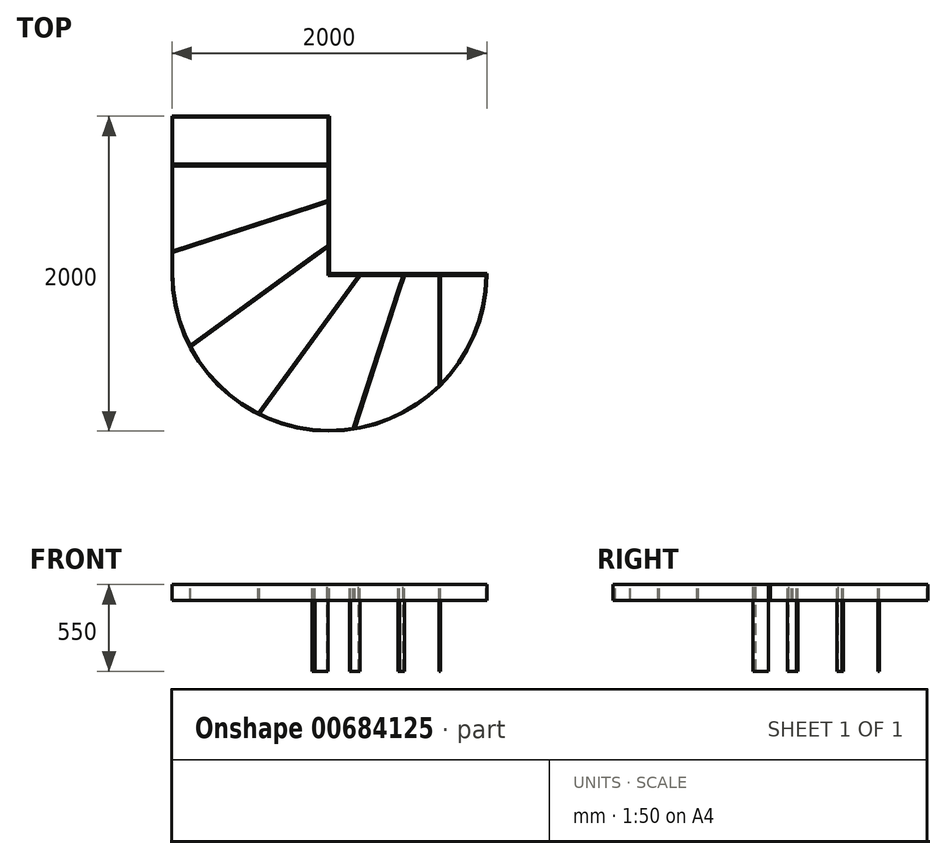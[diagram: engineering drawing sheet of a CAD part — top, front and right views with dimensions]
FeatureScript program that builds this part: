
annotation { "Feature Type Name" : "Feature", "Feature Type Description" : "" }
export const myFeature = defineFeature(function(context is Context, id is Id, definition is map)
    precondition{}
    {
        {
            var Q0;
            Q0=qCreatedBy(makeId("Top.planeOp"),FACE);
            var sketch = newSketch(context, id + "F0", { "sketchPlane" : qUnion([Q0])});
            skLineSegment(sketch, "E0", {"start": v(0, 0) * mm, "end": v(-1000, 0) * mm});
            skLineSegment(sketch, "E1", {"start": v(-1000, 0) * mm, "end": v(-1000, -1000) * mm});
            skLineSegment(sketch, "E2", {"start": v(0, 0) * mm, "end": v(0, -1000) * mm});
            skLineSegment(sketch, "E3", {"start": v(0, -1000) * mm, "end": v(1000, -1000) * mm});
            skArc(sketch, "E4", {"start": v(-1000, -1000) * mm, "mid": v(0, -2000) * mm, "end": v(1000, -1000) * mm});
            skLineSegment(sketch, "E5", {"start": v(-1000, -1000) * mm, "end": v(0, -1000) * mm, "construction": true});
            skLineSegment(sketch, "E6.0", {"start": v(-10, -1010) * mm, "end": v(1000, -1010) * mm});
            skLineSegment(sketch, "E6.1", {"start": v(-10, 0) * mm, "end": v(-10, -1010) * mm});
            skArc(sketch, "E7.0", {"start": v(-995, -1000) * mm, "mid": v(-5, -1994.99) * mm, "end": v(994.95, -1010) * mm});
            skLineSegment(sketch, "E7.1", {"start": v(-995, -5) * mm, "end": v(-995, -1000) * mm});
            skLineSegment(sketch, "E7.2", {"start": v(-10, -5) * mm, "end": v(-995, -5) * mm});
            skLineSegment(sketch, "E8", {"start": v(700, -310) * mm, "end": v(0, -310) * mm, "construction": true});
            skLineSegment(sketch, "E9", {"start": v(700, -310) * mm, "end": v(700, -1010) * mm, "construction": true});
            skLineSegment(sketch, "E10", {"start": v(-10, -310) * mm, "end": v(-995, -310) * mm, "construction": true});
            skLineSegment(sketch, "E11", {"start": v(700, -1010) * mm, "end": v(700, -1707.12) * mm, "construction": true});
            skLineSegment(sketch, "E12", {"start": v(700, -310) * mm, "end": v(0, -537.44) * mm, "construction": true});
            skLineSegment(sketch, "E13", {"start": v(700, -310) * mm, "end": v(0, -818.58) * mm, "construction": true});
            skLineSegment(sketch, "E14", {"start": v(700, -310) * mm, "end": v(198.69, -1000) * mm, "construction": true});
            skLineSegment(sketch, "E15", {"start": v(700, -310) * mm, "end": v(475.8, -1000) * mm, "construction": true});
            skLineSegment(sketch, "E16.0", {"start": v(-10, -305) * mm, "end": v(-995, -305) * mm});
            skLineSegment(sketch, "E17.0", {"start": v(-10, -315) * mm, "end": v(-995, -315) * mm});
            skLineSegment(sketch, "E18", {"start": v(0, -537.44) * mm, "end": v(-995, -860.74) * mm, "construction": true});
            skLineSegment(sketch, "E19", {"start": v(0, -818.58) * mm, "end": v(-882.44, -1459.7) * mm, "construction": true});
            skLineSegment(sketch, "E20", {"start": v(198.69, -1000) * mm, "end": v(-447.12, -1888.88) * mm, "construction": true});
            skLineSegment(sketch, "E21", {"start": v(475.8, -1000) * mm, "end": v(156.54, -1982.6) * mm, "construction": true});
            skLineSegment(sketch, "E22.0", {"start": v(-10, -535.44) * mm, "end": v(-995, -855.48) * mm});
            skLineSegment(sketch, "E23.0", {"start": v(-10, -545.95) * mm, "end": v(-995, -866) * mm});
            skLineSegment(sketch, "E24.0", {"start": v(-10, -819.66) * mm, "end": v(-884.76, -1455.22) * mm});
            skLineSegment(sketch, "E25.0", {"start": v(-10, -832.03) * mm, "end": v(-880.1, -1464.18) * mm});
            skLineSegment(sketch, "E26.0", {"start": v(197.6, -1010) * mm, "end": v(-442.59, -1891.15) * mm});
            skLineSegment(sketch, "E27.0", {"start": v(467.3, -1010) * mm, "end": v(151, -1983.48) * mm});
            skLineSegment(sketch, "E28.0", {"start": v(477.81, -1010) * mm, "end": v(162.09, -1981.7) * mm});
            skLineSegment(sketch, "E29.0", {"start": v(695, -1010) * mm, "end": v(695, -1712.04) * mm});
            skLineSegment(sketch, "E30.0", {"start": v(705, -1010) * mm, "end": v(705, -1702.14) * mm});
            skLineSegment(sketch, "E31.trimOffspring", {"start": v(185.24, -1010) * mm, "end": v(-451.64, -1886.6) * mm});
            skLineSegment(sketch, "E32", {"start": v(-10, -545.95) * mm, "end": v(-13.1, -536.44) * mm});
            skLineSegment(sketch, "E33", {"start": v(-10, -832.03) * mm, "end": v(-15.88, -823.94) * mm});
            skLineSegment(sketch, "E34", {"start": v(185.24, -1010) * mm, "end": v(193.33, -1015.88) * mm});
            skLineSegment(sketch, "E35", {"start": v(467.3, -1010) * mm, "end": v(476.8, -1013.1) * mm});
            skLineSegment(sketch, "E36", {"start": v(-110, -305) * mm, "end": v(-110, -315) * mm});
            skLineSegment(sketch, "E37", {"start": v(-108.2, -567.34) * mm, "end": v(-105.1, -576.85) * mm});
            skLineSegment(sketch, "E38", {"start": v(-96.78, -882.71) * mm, "end": v(-90.9, -890.8) * mm});
            skLineSegment(sketch, "E39", {"start": v(126.46, -1090.9) * mm, "end": v(134.55, -1096.78) * mm});
            skLineSegment(sketch, "E40", {"start": v(436.4, -1105.1) * mm, "end": v(445.9, -1108.2) * mm});
            skLineSegment(sketch, "E41", {"start": v(695, -1110) * mm, "end": v(705, -1110) * mm});
            skSolve(sketch);
        }
        {
            var Q0;
            {var subQ9=sQuery(id+"F0.wireOp",EDGE,"E2");Q0=makeQuery(id+"F0.imprint","IMPRINT",FACE,{"disambiguationData":[TD([[makeQuery(id+"F0.imprint","IMPRINT",EDGE,{"derivedFrom":subQ9}),-1.0]])]});}
            extrude(context, id + "F1", {"entities" : qUnion([Q0]), "oppositeDirection" : true, "depth" : 100 * mm, "offsetDistance" : 25 * mm});
        }
        {
            var Q0;
            {var subQ4=sQuery(id+"F0.wireOp",EDGE,"E1");Q0=makeQuery(id+"F0.imprint","IMPRINT",FACE,{"disambiguationData":[TD([[makeQuery(id+"F0.imprint","IMPRINT",EDGE,{"derivedFrom":subQ4}),1.0]])]});}
            extrude(context, id + "F2", {"entities" : qUnion([Q0]), "oppositeDirection" : true, "depth" : 100 * mm, "offsetDistance" : 25 * mm});
        }
        {
            var Q0;
            {var subQ5=sQuery(id+"F0.wireOp",EDGE,"E36");Q0=makeQuery(id+"F0.imprint","IMPRINT",FACE,{"disambiguationData":[TD([[makeQuery(id+"F0.imprint","IMPRINT",EDGE,{"derivedFrom":subQ5}),1.0]])]});}
            var Q1;
            {var subQ0=sQuery(id+"F0.wireOp",EDGE,"E32");Q1=makeQuery(id+"F0.imprint","IMPRINT",FACE,{"disambiguationData":[TD([[makeQuery(id+"F0.imprint","IMPRINT",EDGE,{"derivedFrom":subQ0}),1.0]])]});}
            var Q2;
            {var subQ0=sQuery(id+"F0.wireOp",EDGE,"E33");Q2=makeQuery(id+"F0.imprint","IMPRINT",FACE,{"disambiguationData":[TD([[makeQuery(id+"F0.imprint","IMPRINT",EDGE,{"derivedFrom":subQ0}),1.0]])]});}
            var Q3;
            {var subQ0=sQuery(id+"F0.wireOp",EDGE,"E34");Q3=makeQuery(id+"F0.imprint","IMPRINT",FACE,{"disambiguationData":[TD([[makeQuery(id+"F0.imprint","IMPRINT",EDGE,{"derivedFrom":subQ0}),-1.0]])]});}
            var Q4;
            {var subQ0=sQuery(id+"F0.wireOp",EDGE,"E35");Q4=makeQuery(id+"F0.imprint","IMPRINT",FACE,{"disambiguationData":[TD([[makeQuery(id+"F0.imprint","IMPRINT",EDGE,{"derivedFrom":subQ0}),-1.0]])]});}
            var Q5;
            {var subQ5=sQuery(id+"F0.wireOp",EDGE,"E41");Q5=makeQuery(id+"F0.imprint","IMPRINT",FACE,{"disambiguationData":[TD([[makeQuery(id+"F0.imprint","IMPRINT",EDGE,{"derivedFrom":subQ5}),1.0]])]});}
            extrude(context, id + "F3", {"entities" : qUnion([Q0, Q1, Q2, Q3, Q4, Q5]), "operationType" : NewBodyOperationType.ADD, "oppositeDirection" : true, "depth" : 550 * mm, "offsetDistance" : 25 * mm});
        }
        {
            var Q0;
            {var subQ5=sQuery(id+"F0.wireOp",EDGE,"E36");Q0=makeQuery(id+"F0.imprint","IMPRINT",FACE,{"disambiguationData":[TD([[makeQuery(id+"F0.imprint","IMPRINT",EDGE,{"derivedFrom":subQ5}),-1.0]])]});}
            var Q1;
            {var subQ5=sQuery(id+"F0.wireOp",EDGE,"E37");Q1=makeQuery(id+"F0.imprint","IMPRINT",FACE,{"disambiguationData":[TD([[makeQuery(id+"F0.imprint","IMPRINT",EDGE,{"derivedFrom":subQ5}),-1.0]])]});}
            var Q2;
            {var subQ5=sQuery(id+"F0.wireOp",EDGE,"E38");Q2=makeQuery(id+"F0.imprint","IMPRINT",FACE,{"disambiguationData":[TD([[makeQuery(id+"F0.imprint","IMPRINT",EDGE,{"derivedFrom":subQ5}),-1.0]])]});}
            var Q3;
            {var subQ5=sQuery(id+"F0.wireOp",EDGE,"E39");Q3=makeQuery(id+"F0.imprint","IMPRINT",FACE,{"disambiguationData":[TD([[makeQuery(id+"F0.imprint","IMPRINT",EDGE,{"derivedFrom":subQ5}),-1.0]])]});}
            var Q4;
            {var subQ5=sQuery(id+"F0.wireOp",EDGE,"E40");Q4=makeQuery(id+"F0.imprint","IMPRINT",FACE,{"disambiguationData":[TD([[makeQuery(id+"F0.imprint","IMPRINT",EDGE,{"derivedFrom":subQ5}),-1.0]])]});}
            var Q5;
            {var subQ5=sQuery(id+"F0.wireOp",EDGE,"E41");Q5=makeQuery(id+"F0.imprint","IMPRINT",FACE,{"disambiguationData":[TD([[makeQuery(id+"F0.imprint","IMPRINT",EDGE,{"derivedFrom":subQ5}),-1.0]])]});}
            extrude(context, id + "F4", {"entities" : qUnion([Q0, Q1, Q2, Q3, Q4, Q5]), "oppositeDirection" : true, "depth" : 100 * mm, "offsetDistance" : 25 * mm});
        }
    });
